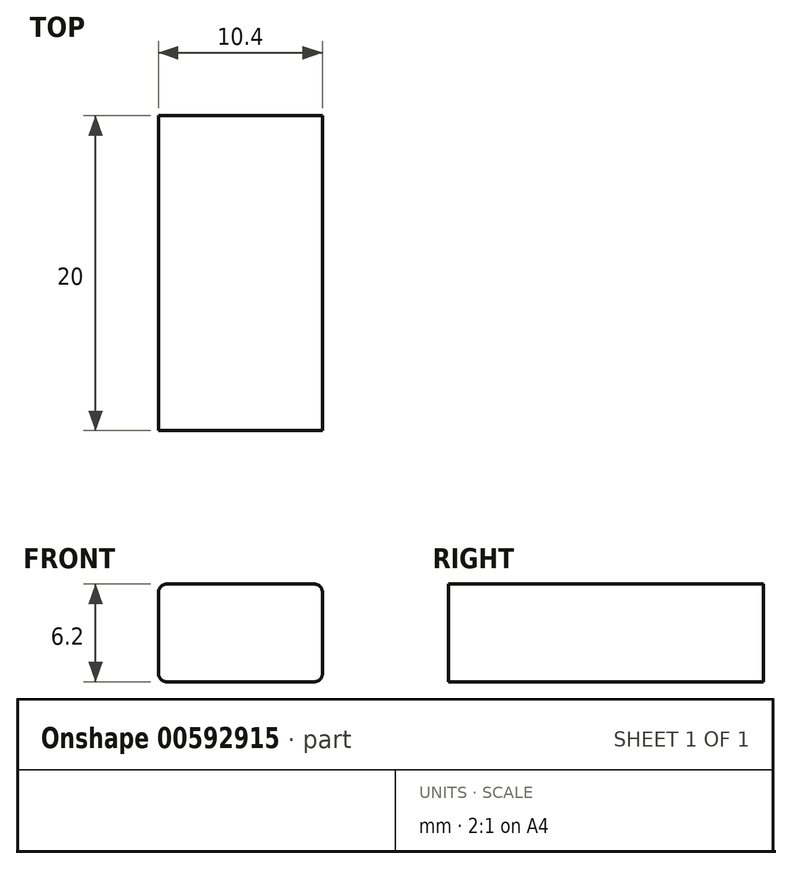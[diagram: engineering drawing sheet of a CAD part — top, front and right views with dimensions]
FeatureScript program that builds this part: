
annotation { "Feature Type Name" : "Feature", "Feature Type Description" : "" }
export const myFeature = defineFeature(function(context is Context, id is Id, definition is map)
    precondition{}
    {
        {
            var Q0;
            Q0=qCreatedBy(makeId("Front.planeOp"),FACE);
            var sketch = newSketch(context, id + "F0", { "sketchPlane" : qUnion([Q0])});
            skLineSegment(sketch, "E0.bottom", {"start": v(0.5, 0) * mm, "end": v(9.9, 0) * mm});
            skLineSegment(sketch, "E0.top", {"start": v(0.5, -6.2) * mm, "end": v(9.9, -6.2) * mm});
            skLineSegment(sketch, "E0.left", {"start": v(0, -0.5) * mm, "end": v(0, -5.7) * mm});
            skLineSegment(sketch, "E0.right", {"start": v(10.4, -0.5) * mm, "end": v(10.4, -5.7) * mm});
            skPoint(sketch, "E1.visualSharp", {"position": v(0, 0) * mm});
            skArc(sketch, "E1.filletArc", {"start": v(0.5, 0) * mm, "mid": v(0.15, -0.15) * mm, "end": v(0, -0.5) * mm});
            skPoint(sketch, "E2.visualSharp", {"position": v(0, -6.2) * mm});
            skArc(sketch, "E2.filletArc", {"start": v(0, -5.7) * mm, "mid": v(0.15, -6.05) * mm, "end": v(0.5, -6.2) * mm});
            skPoint(sketch, "E3.visualSharp", {"position": v(10.4, -6.2) * mm});
            skArc(sketch, "E3.filletArc", {"start": v(9.9, -6.2) * mm, "mid": v(10.25, -6.05) * mm, "end": v(10.4, -5.7) * mm});
            skPoint(sketch, "E4.visualSharp", {"position": v(10.4, 0) * mm});
            skArc(sketch, "E4.filletArc", {"start": v(10.4, -0.5) * mm, "mid": v(10.25, -0.15) * mm, "end": v(9.9, 0) * mm});
            skSolve(sketch);
        }
        {
            var Q0;
            Q0 = qSketchRegion(id + "F0", true);
            extrude(context, id + "F1", {"entities" : qUnion([Q0]), "depth" : 20 * mm, "offsetDistance" : 25 * mm});
        }
    });
